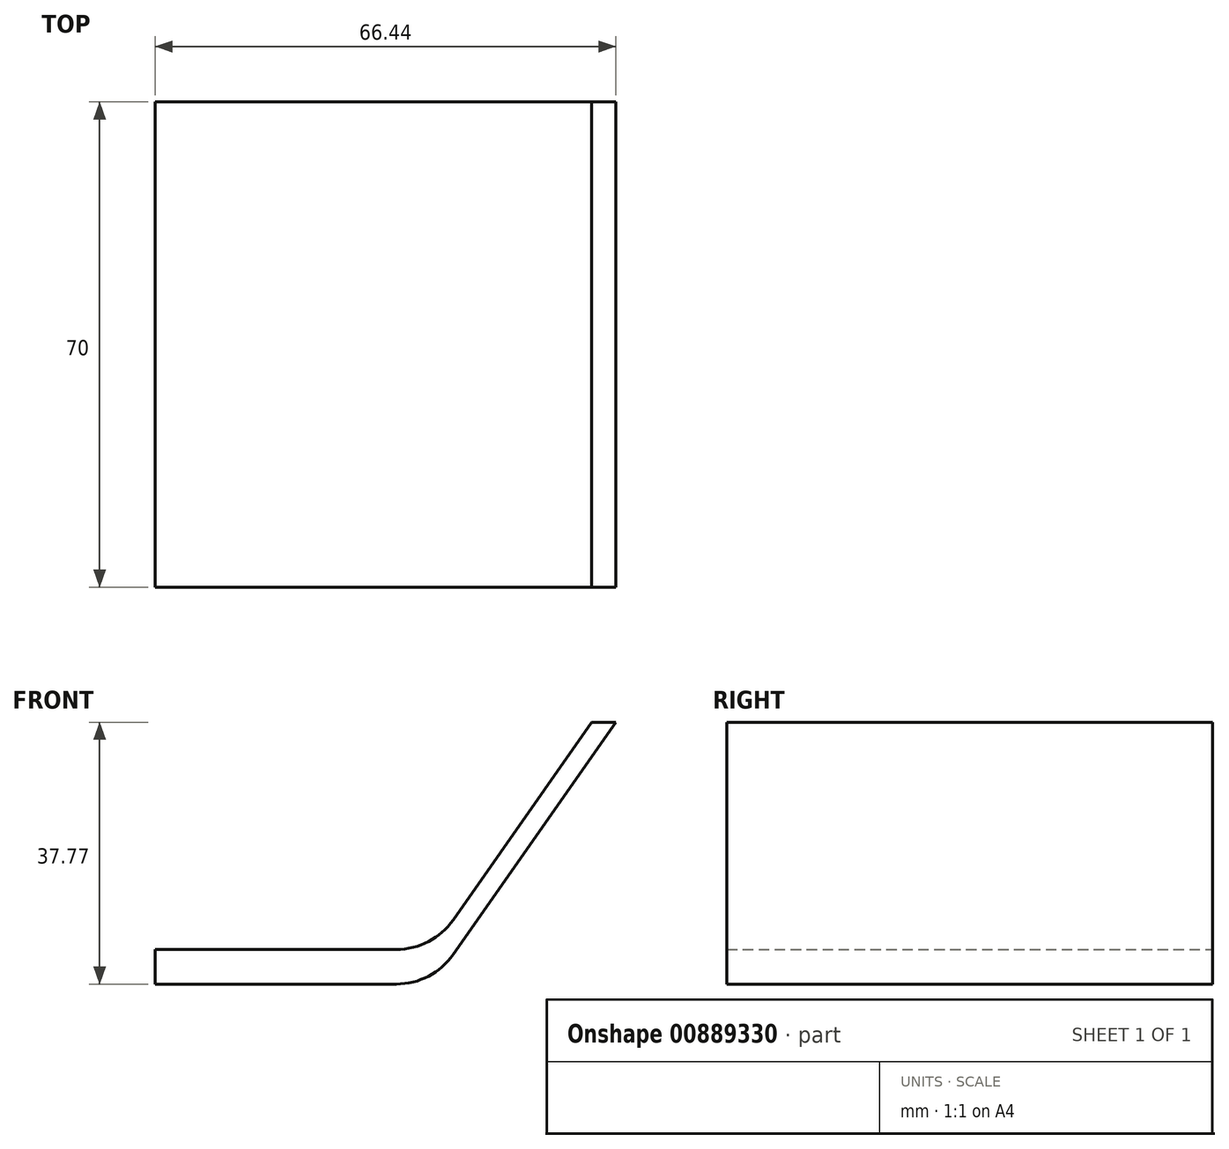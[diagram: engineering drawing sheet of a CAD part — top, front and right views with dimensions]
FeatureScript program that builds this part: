
annotation { "Feature Type Name" : "Feature", "Feature Type Description" : "" }
export const myFeature = defineFeature(function(context is Context, id is Id, definition is map)
    precondition{}
    {
        {
            var Q0;
            Q0=qCreatedBy(makeId("Top.planeOp"),FACE);
            var sketch = newSketch(context, id + "F0", { "sketchPlane" : qUnion([Q0])});
            skLineSegment(sketch, "E0.bottom", {"start": v(20, -35) * mm, "end": v(-20, -35) * mm});
            skLineSegment(sketch, "E0.top", {"start": v(20, 35) * mm, "end": v(-20, 35) * mm});
            skLineSegment(sketch, "E0.left", {"start": v(20, -35) * mm, "end": v(20, 35) * mm});
            skLineSegment(sketch, "E0.right", {"start": v(-20, -35) * mm, "end": v(-20, 35) * mm});
            skPoint(sketch, "E0.middle", {"position": v(0, 0) * mm});
            skSolve(sketch);
        }
        {
            var Q0;
            Q0 = qSketchRegion(id + "F0", true);
            extrude(context, id + "F1", {"entities" : qUnion([Q0]), "depth" : 5 * mm, "offsetDistance" : 25 * mm});
        }
        {
            var Q0;
            Q0=qCreatedBy(makeId("Front.planeOp"),FACE);
            var sketch = newSketch(context, id + "F2", { "sketchPlane" : qUnion([Q0])});
            skLineSegment(sketch, "E1", {"start": v(20, 5) * mm, "end": v(42.94, 37.77) * mm});
            skLineSegment(sketch, "E2", {"start": v(46.44, 37.77) * mm, "end": v(20, 0) * mm});
            skLineSegment(sketch, "E3", {"start": v(20, 0) * mm, "end": v(20, 5) * mm});
            skLineSegment(sketch, "E4", {"start": v(42.94, 37.77) * mm, "end": v(46.44, 37.77) * mm});
            skSolve(sketch);
        }
        {
            var Q0;
            Q0 = qSketchRegion(id + "F2", true);
            extrude(context, id + "F3", {"entities" : qUnion([Q0]), "operationType" : NewBodyOperationType.ADD, "endBound" : BoundingType.SYMMETRIC, "depth" : 70 * mm, "offsetDistance" : 25 * mm});
        }
        {
            var Q0;
            Q0=makeQuery(id+"F3.boolean.opBoolean","MERGE",EDGE,{"derivedFrom":[makeQuery(id+"F1.opExtrude","CAP_EDGE",EDGE,{"disambiguationData":[OSD([sQuery(id+"F0.wireOp",EDGE,"E0.left")])],"isStart":false}),makeQuery(id+"F3.opExtrude","SWEPT_EDGE",EDGE,{"disambiguationData":[OSD([sQuery(id+"F2.wireOp",EDGE,"E1"),sQuery(id+"F2.wireOp",EDGE,"E3")])]})]});
            var Q1;
            Q1=makeQuery(id+"F3.boolean.opBoolean","MERGE",EDGE,{"derivedFrom":[makeQuery(id+"F1.opExtrude","CAP_EDGE",EDGE,{"disambiguationData":[OSD([sQuery(id+"F0.wireOp",EDGE,"E0.left")])],"isStart":true}),makeQuery(id+"F3.opExtrude","SWEPT_EDGE",EDGE,{"disambiguationData":[OSD([sQuery(id+"F2.wireOp",EDGE,"E2"),sQuery(id+"F2.wireOp",EDGE,"E3")])]})]});
            fillet(context, id + "F4", {"entities" : qUnion([Q0, Q1]), "radius" : 10 * mm, "tangentPropagation" : true, "allowEdgeOverflow" : false});
        }
    });
